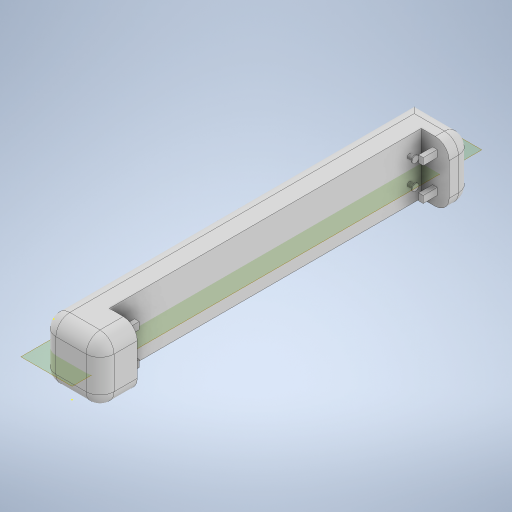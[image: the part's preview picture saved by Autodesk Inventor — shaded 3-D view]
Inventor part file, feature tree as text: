
AUTODESK INVENTOR PART (.ipt)
format: ipt  version: 2023 (Build 270158000, 158)  size: 371,200 bytes
history: native  units: mm
features: sketch x10, extrude x9, plane x7, mirror x4, other x1, fillet x1
ambient origin geometry x8: Origin, YZ Plane, XZ Plane, XY Plane, X Axis, Y Axis, Z Axis, Center Point
bodies: Solid1 (feature_tree)
feature tree (32):
  other  "plane body"
  extrude  "Extrusion1"  Depth=800.0mm
  extrude  "Extrusion2"  Depth=60.0mm
  extrude  "Extrusion3"  Depth=50.0mm
  extrude  "Extrusion4"  Depth=10.0mm
  plane  "Work Plane1"
  mirror  "Mirror1"
  plane  "Work Plane3"
  mirror  "Mirror2"
  sketch  "Sketch5"  dims[d7=1000.0mm d8=0.0mm d10=10.0mm]
  sketch  "Sketch6"  dims[d11=15.0mm d12=30.0mm d13=0.0mm]
  extrude  "Extrusion5"  Depth=30.0mm TaperAngle=0.0deg
  extrude  "Extrusion6"  Depth=30.0mm TaperAngle=0.0deg
  mirror  "Mirror3"
  plane  "Work Plane5"
  mirror  "Mirror4"
  extrude  "Extrusion7"  Depth=335.0mm
  extrude  "Extrusion8"  Depth=39.0mm
  extrude  "Extrusion9"  Depth=10.5mm TaperAngle=0.0deg
  fillet  "Fillet1"  Radius=15.0mm
  sketch  "Sketch1"  dims[d0=130.0mm d1=800.0mm]
  sketch  "Sketch2"  dims[d2=100.0mm d3=0.0mm d4=60.0mm]
  sketch  "Sketch4"  dims[d5=80.0mm d6=50.0mm]
  plane  "Work Plane2"
  sketch  "Sketch7"  dims[d14=20.071286mm d15=30.0mm d16=0.0mm]
  sketch  "Sketch8"  dims[d17=-65.0mm d18=335.0mm]
  plane  "Work Plane4"
  plane  "Work Plane6"
  plane  "Work Plane7"
  sketch  "Sketch9"  dims[d19=25.0mm d20=39.0mm]
  sketch  "Sketch11"  dims[d21=10.0mm d22=10.5mm d23=0.0mm d24=15.0mm]
  sketch  "Sketch12"  dims[d25=2.0mm d26=0.0mm d27=335.0mm d28=61.0mm d29=50.0mm d30=8.0mm d31=50.0mm d32=0.0mm d33=25.0mm d34=25.0mm d35=10.0mm d36=8.0mm d37=0.0mm d38=25.0mm d39=0.0mm d40=5.0mm d41=260.0mm d42=10.0mm d43=55.0mm d44=0.0mm d45=30.0mm d46=0.0mm d47=0.0mm d48=0.0mm]
